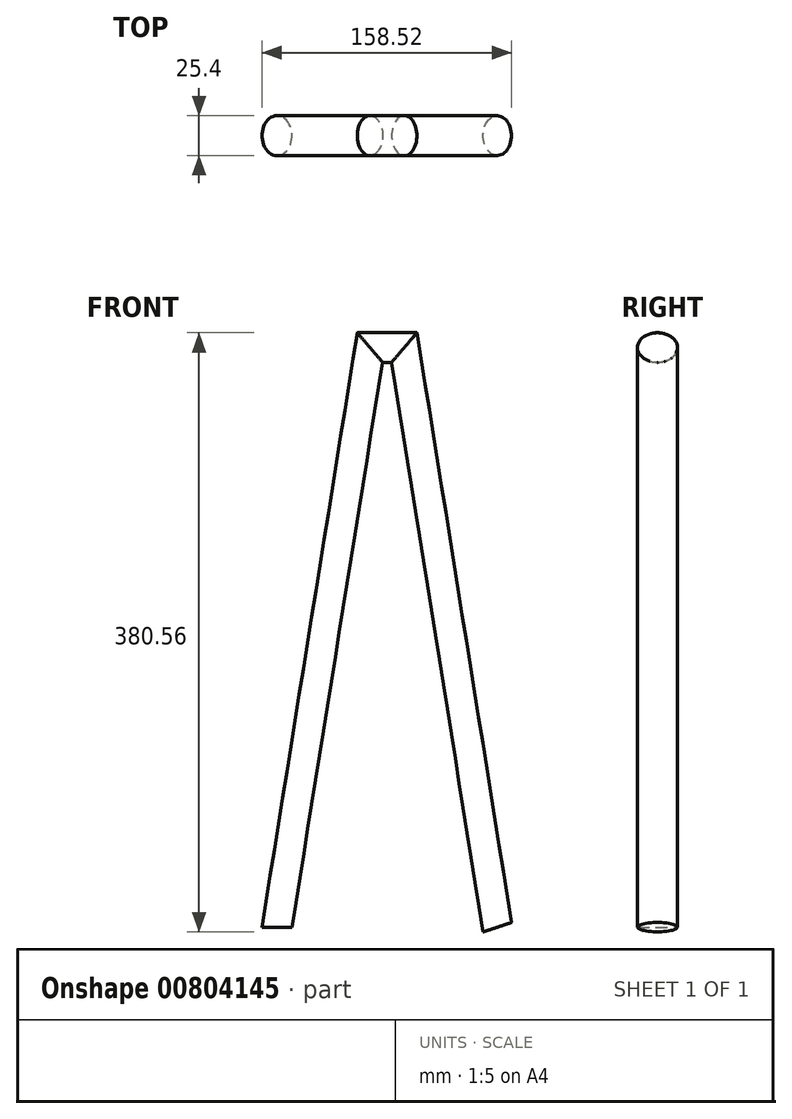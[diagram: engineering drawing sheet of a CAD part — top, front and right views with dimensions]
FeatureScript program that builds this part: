
annotation { "Feature Type Name" : "Feature", "Feature Type Description" : "" }
export const myFeature = defineFeature(function(context is Context, id is Id, definition is map)
    precondition{}
    {
        {
            var Q0;
            Q0=qCreatedBy(makeId("Front.planeOp"),FACE);
            var sketch = newSketch(context, id + "F0", { "sketchPlane" : qUnion([Q0])});
            skLineSegment(sketch, "E0", {"start": v(0, 0) * mm, "end": v(0, 223.39) * mm, "construction": true});
            skLineSegment(sketch, "E1", {"start": v(0, 223.39) * mm, "end": v(-19.05, 223.39) * mm, "construction": true});
            skLineSegment(sketch, "E2", {"start": v(-19.05, 223.39) * mm, "end": v(-79.38, -152.8) * mm, "construction": true});
            skLineSegment(sketch, "E3", {"start": v(-79.38, -152.8) * mm, "end": v(0, -152.8) * mm, "construction": true});
            skLineSegment(sketch, "E4.MirrorCS", {"start": v(19.05, 223.39) * mm, "end": v(79.38, -152.8) * mm, "construction": true});
            skLineSegment(sketch, "E5.MirrorCS", {"start": v(0, 223.39) * mm, "end": v(19.05, 223.39) * mm, "construction": true});
            skLineSegment(sketch, "E6.0", {"start": v(10.93, 213.86) * mm, "end": v(69.97, -154.32) * mm});
            skLineSegment(sketch, "E7.0", {"start": v(-10.93, 213.86) * mm, "end": v(-69.97, -154.32) * mm});
            skLineSegment(sketch, "E8.0", {"start": v(0, 213.86) * mm, "end": v(10.93, 213.86) * mm});
            skLineSegment(sketch, "E8.1", {"start": v(0, 213.86) * mm, "end": v(-10.93, 213.86) * mm});
            skSolve(sketch);
        }
        {
            var Q0;
            Q0=qCreatedBy(makeId("Front.planeOp"),FACE);
            var sketch = newSketch(context, id + "F1", { "sketchPlane" : qUnion([Q0])});
            skLineSegment(sketch, "E9.0", {"start": v(-10.93, 213.86) * mm, "end": v(-69.97, -154.32) * mm, "construction": true});
            skLineSegment(sketch, "E10", {"start": v(0, 0) * mm, "end": v(-45.22, 0) * mm, "construction": true});
            skSolve(sketch);
        }
        {
            var Q0;
            Q0=qCreatedBy(makeId("Top.planeOp"),FACE);
            var sketch = newSketch(context, id + "F2", { "sketchPlane" : qUnion([Q0])});
            skPoint(sketch, "E11.0", {"position": v(-45.22, 0) * mm});
            skEllipse(sketch, "E12", {"center": v(-45.22, 0) * mm, "majorRadius": 12.7 * mm, "minorRadius": 9.53 * mm, "majorAxis": v(0, -1)});
            skSolve(sketch);
        }
        {
            var Q0;
            Q0=makeQuery(id+"F2.imprint","IMPRINT",FACE,{"disambiguationData":[TD([[makeQuery(id+"F2.imprint","IMPRINT",EDGE,{"derivedFrom":sQuery(id+"F2.wireOp",EDGE,"E12")}),1.0]])]});
            var Q1;
            Q1=sQuery(id+"F0.wireOp",EDGE,"E7.0");
            var Q2;
            Q2=sQuery(id+"F0.wireOp",EDGE,"E8.1");
            var Q3;
            Q3=sQuery(id+"F0.wireOp",EDGE,"E8.0");
            var Q4;
            Q4=sQuery(id+"F0.wireOp",EDGE,"E6.0");
            sweep(context, id + "F3", {"profiles" : qUnion([Q0]), "path" : qUnion([Q1, Q2, Q3, Q4])});
        }
    });
